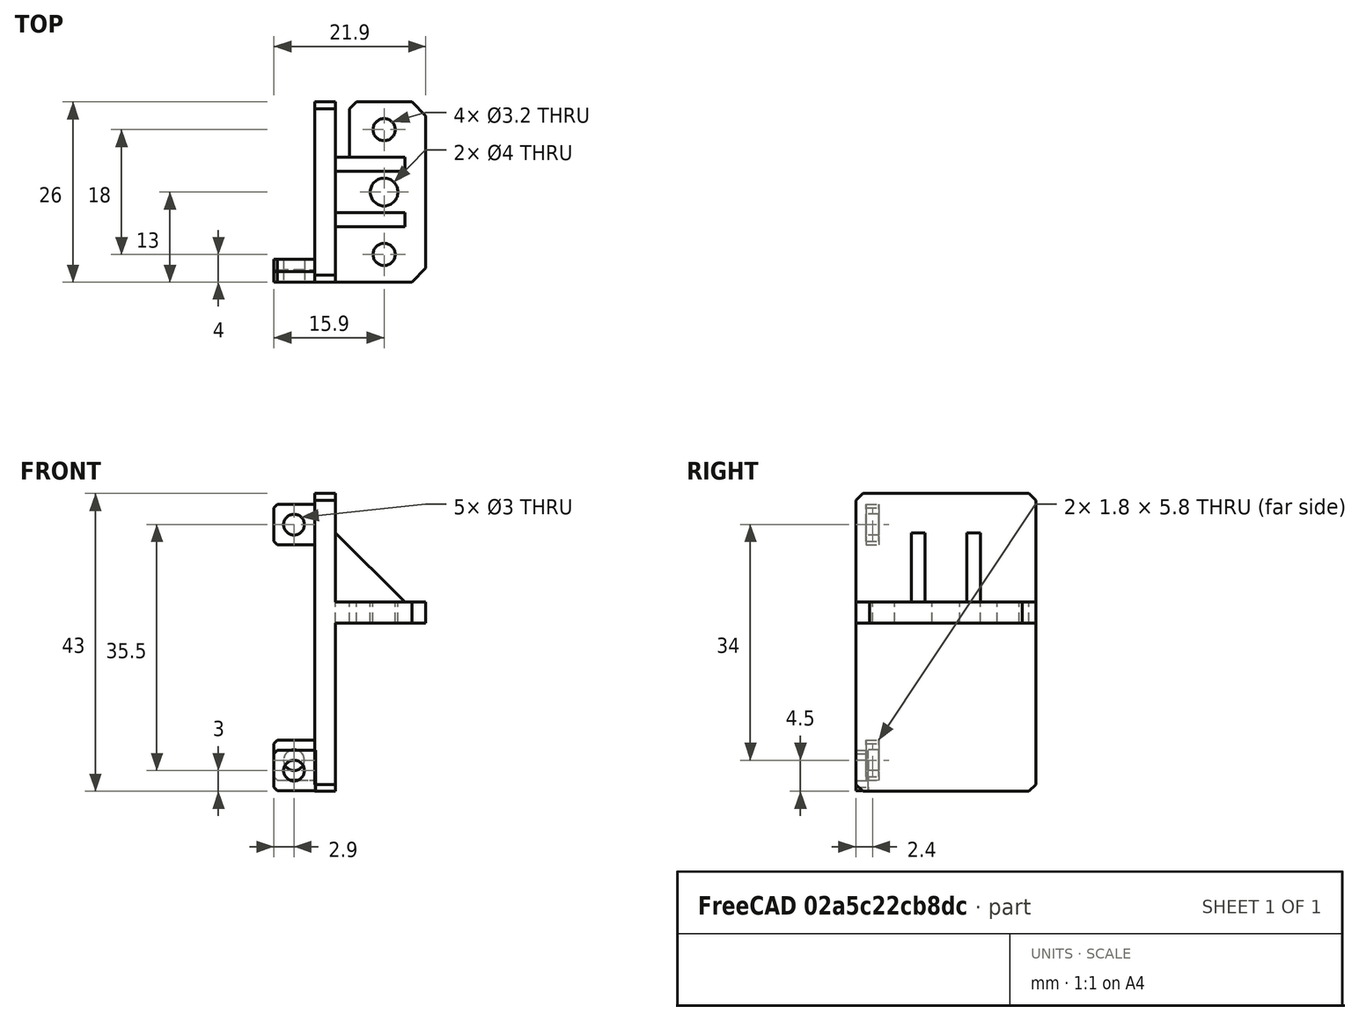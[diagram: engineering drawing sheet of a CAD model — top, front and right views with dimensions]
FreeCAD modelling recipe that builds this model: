
FCSTD DOCUMENT  (FreeCAD 0.18R14555 (Git shallow))
Label: hemera-fixed-bltouch-mount
License: All rights reserved
LicenseURL: http://en.wikipedia.org/wiki/All_rights_reserved
objects: Part::Feature×6, Part::Box×4, Part::Cylinder×4, Part::Chamfer×4, Part::MultiFuse×3, Part::Cut×3
note: 24 computed .brp shape members not serialized (recipe doc carries the construction recipe); baked Part::Feature solids carry a one-line shape summary decoded from their .brp

FEATURE [Part::Box] Box  label="Cube"
  AttacherType = Attacher::AttachEngine3D
  Height = 3
  Length = 13
  Placement = pos=(3,0,24.3) rot=(0,0,1;0rad)
  Width = 26
FEATURE [Part::Box] Box001  label="Cube001"
  AttacherType = Attacher::AttachEngine3D
  Height = 43
  Length = 3
  Width = 26
FEATURE [Part::Cylinder] Cylinder
  Angle = 360
  AttacherType = Attacher::AttachEngine3D
  Height = 5
  Placement = pos=(10,4,23) rot=(0,0,1;0rad)
  Radius = 1.6
FEATURE [Part::Cylinder] Cylinder001
  Angle = 360
  AttacherType = Attacher::AttachEngine3D
  Height = 5
  Placement = pos=(10,22,23) rot=(0,0,1;0rad)
  Radius = 1.6
FEATURE [Part::Cylinder] Cylinder002
  Angle = 360
  AttacherType = Attacher::AttachEngine3D
  Height = 5
  Placement = pos=(10,13,23) rot=(0,0,1;0rad)
  Radius = 2
FEATURE [Part::Feature] Body001
  Placement = pos=(23,10,27.3) rot=(0,0,1;0rad)
  shape: bbox 10 x 2 x 10 mm, 5 faces (baked)
FEATURE [Part::Feature] Body002
  Placement = pos=(23,18,27.3) rot=(0,0,1;0rad)
  shape: bbox 10 x 2 x 10 mm, 5 faces (baked)
FEATURE [Part::MultiFuse] Fusion
  Shapes = -> [Cylinder,Cylinder001,Cylinder002]
FEATURE [Part::Cut] Cut
  Base = -> Box
  Tool = -> Fusion
FEATURE [Part::MultiFuse] Fusion001
  Shapes = -> [Cut,Box001,Body001,Body002]
FEATURE [Part::Chamfer] Chamfer
  Base = -> Fusion001
  Edges = 2 edges r=2: [Edge19,Edge31]
FEATURE [Part::Box] Box002  label="Cube002"
  AttacherType = Attacher::AttachEngine3D
  Height = 5.8
  Length = 6
  Placement = pos=(-5.9,0,0.1) rot=(0,0,1;0rad)
  Width = 1.8
FEATURE [Part::Cylinder] Cylinder003
  Angle = 360
  AttacherType = Attacher::AttachEngine3D
  Height = 10
  Placement = pos=(-3,6,3) rot=(1,0,0;1.5708rad)
  Radius = 1.5
FEATURE [Part::Cut] Cut001
  Base = -> Box002
  Tool = -> Cylinder003
FEATURE [Part::Chamfer] Chamfer001
  Base = -> Cut001
  Edges = 2 edges r=0.5: [Edge2,Edge4]
FEATURE [Part::Feature] Chamfer001001  label="Chamfer002"
  Placement = pos=(0,1.5,1.5) rot=(0,0,1;0rad)
  shape: bbox 6 x 1.8 x 5.8 mm, 9 faces (baked)
FEATURE [Part::Feature] Chamfer001002  label="Chamfer003"
  Placement = pos=(0,1.5,35.5) rot=(0,0,1;0rad)
  shape: bbox 6 x 1.8 x 5.8 mm, 9 faces (baked)
FEATURE [Part::Chamfer] Chamfer001003
  Base = -> Chamfer
  Edges = 4 edges r=1: [Edge15,Edge18,Edge44,Edge54]
FEATURE [Part::MultiFuse] Fusion002
  Shapes = -> [Chamfer001002,Chamfer001001,Chamfer001003]
FEATURE [Part::Box] Box003  label="Cube003"
  AttacherType = Attacher::AttachEngine3D
  Height = 8
  Length = 2
  Placement = pos=(3,18,22.5) rot=(0,0,1;0rad)
  Width = 8
FEATURE [Part::Cut] Cut002
  Base = -> Fusion002
  Tool = -> Box003
FEATURE [Part::Chamfer] Chamfer001004
  Base = -> Cut002
  Edges = 1 edges r=1: [Edge125]
FEATURE [Part::Feature] Chamfer001004001  label="Chamfer001005"
  shape: bbox 21.9 x 26 x 43 mm, 43 faces (baked)
FEATURE [Part::Feature] Chamfer001004001001  label="Chamfer001006"
  shape: bbox 21.9 x 26 x 43 mm, 43 faces (baked)
